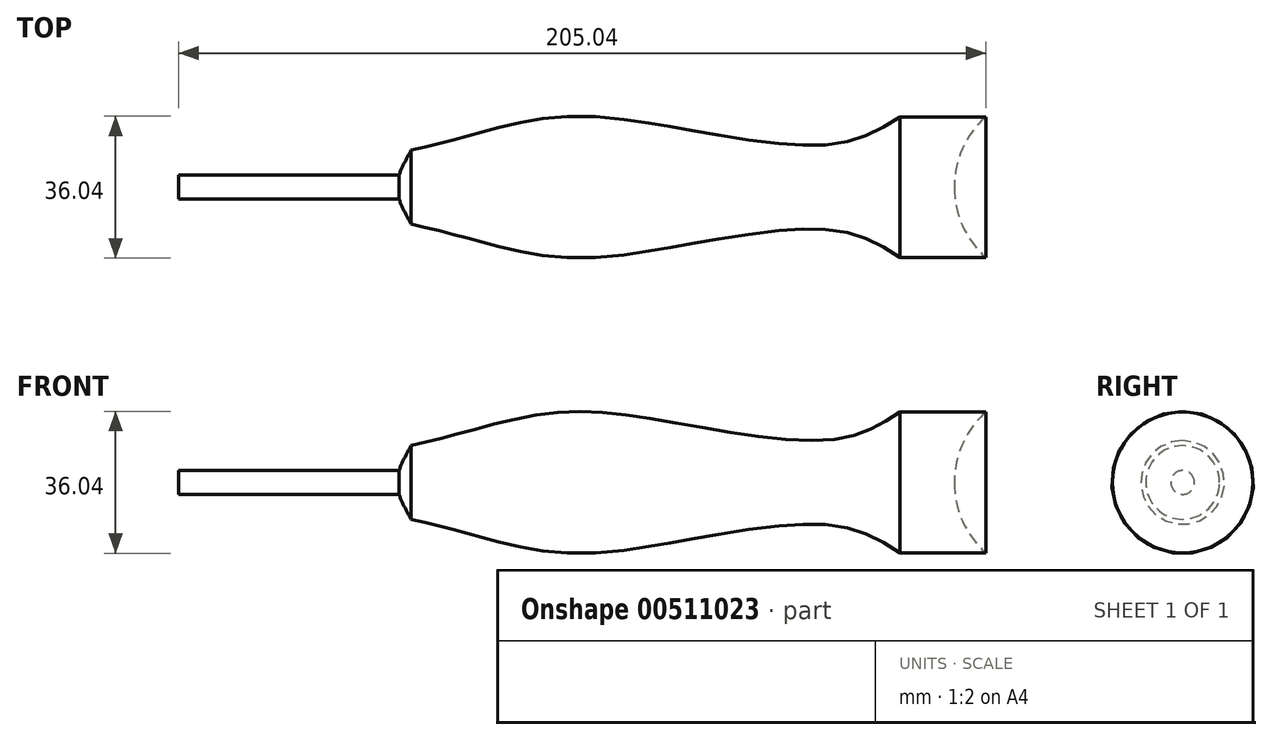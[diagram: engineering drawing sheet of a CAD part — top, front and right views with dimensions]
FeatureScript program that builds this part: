
annotation { "Feature Type Name" : "Feature", "Feature Type Description" : "" }
export const myFeature = defineFeature(function(context is Context, id is Id, definition is map)
    precondition{}
    {
        {
            var Q0;
            Q0=qCreatedBy(makeId("Front.planeOp"),FACE);
            var sketch = newSketch(context, id + "F0", { "sketchPlane" : qUnion([Q0])});
            skLineSegment(sketch, "E0", {"start": v(-81.44, 0) * mm, "end": v(68.56, 0) * mm});
            skArc(sketch, "E1", {"start": v(76.55, 17.86) * mm, "mid": v(70.64, 9.78) * mm, "end": v(68.56, 0) * mm});
            skLineSegment(sketch, "E2", {"start": v(76.55, 17.86) * mm, "end": v(54.76, 17.86) * mm});
            skLineSegment(sketch, "E3", {"start": v(-72.54, 3.01) * mm, "end": v(-128.49, 3.01) * mm});
            skLineSegment(sketch, "E4", {"start": v(-81.44, 0) * mm, "end": v(-128.49, 0) * mm});
            skLineSegment(sketch, "E5", {"start": v(-128.49, 0) * mm, "end": v(-128.49, 3.01) * mm});
            skArc(sketch, "E6", {"start": v(-69.4, 9.35) * mm, "mid": v(-71.1, 6.24) * mm, "end": v(-72.54, 3.01) * mm});
            skPoint(sketch, "E7.2.internal.orphan", {"position": v(0, 14.73) * mm});
            skPoint(sketch, "E7.3.internal.orphan", {"position": v(-31.48, 17.86) * mm});
            skPoint(sketch, "E7.endDerivative.orphan", {"position": v(-69.1, 8.98) * mm});
            skFitSpline(sketch, "E8", {"points": [v(54.76, 17.86) * mm, v(38.8, 11.04) * mm, v(0, 14.73) * mm, v(-31.48, 17.86) * mm, v(-55.41, 12.9) * mm, v(-69.4, 9.35) * mm], "startDerivative": vector(-81.2, -52) * mm, "endDerivative": vector(-85.17, -20.65) * mm});
            skSolve(sketch);
        }
        {
            var Q0;
            Q0 = qSketchRegion(id + "F0", true);
            var Q1;
            Q1=sQuery(id+"F0.wireOp",EDGE,"E0");
            revolve(context, id + "F1", {"surfaceOperationType" : NewSurfaceOperationType.NEW, "entities" : qUnion([Q0]), "axis" : qUnion([Q1]), "revolveType" : RevolveType.FULL});
        }
    });
